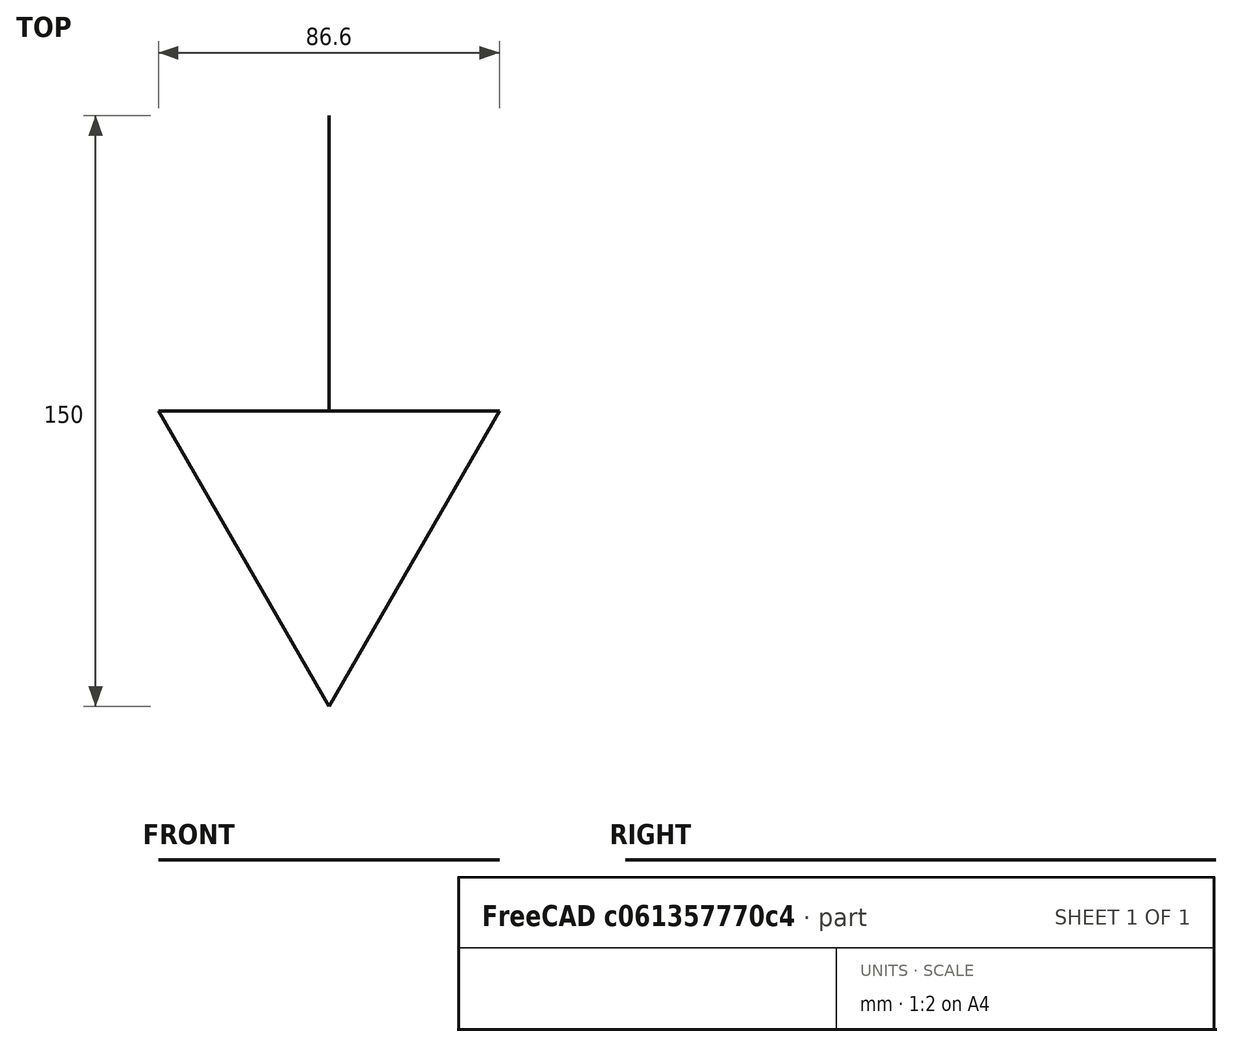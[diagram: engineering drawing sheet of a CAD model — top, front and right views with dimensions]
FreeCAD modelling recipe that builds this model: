
FCSTD DOCUMENT  (FreeCAD 1.1R20260325 (Git shallow))
Label: Tomada_Alta_1modulo_110v_com_simbologia
License: All rights reserved
LicenseURL: http://en.wikipedia.org/wiki/All_rights_reserved
objects: Part::FeaturePython×1, Part::Feature×1, App::DocumentObjectGroup×1
note: 2 computed .brp shape members not serialized (recipe doc carries the construction recipe); baked Part::Feature solids carry a one-line shape summary decoded from their .brp

FEATURE [Part::FeaturePython] Component  label="Tomada_1modulo_110v_alta"  # Arch/BIM 0 (typed FeaturePython)
  HorizontalArea = 0
  IfcData = attributes={"GlobalId": {"name": "GlobalId", "type": "IfcGloballyUniqueId", "is_enum": false, "enum_values": []}, "Description": {"... (+538 chars omitted),+1 more (map truncated)
  IfcType = 0
  MoveBase = false
  MoveWithHost = false
  PerimeterLength = 0
  Placement = pos=(0,0,2250) rot=(0,0,1;0rad)
  PredefinedType = 0
  VerticalArea = 0
FEATURE [Part::Feature] Compound002002002004005002002003003002003005002002005002002002002002002001  label="Simbologia_tomada_alta"
  Placement = pos=(1045.43,2054.32,2240.37) rot=(0,0,-1;1.5708rad)
  shape: bbox 86.6 x 150 x 2e-07 mm, 1 faces, 0 solids (baked)
FEATURE [App::DocumentObjectGroup] Group  label="Tomada_Alta"
  Group = -> [Component,Compound002002002004005002002003003002003005002002005002002002002002002001]
